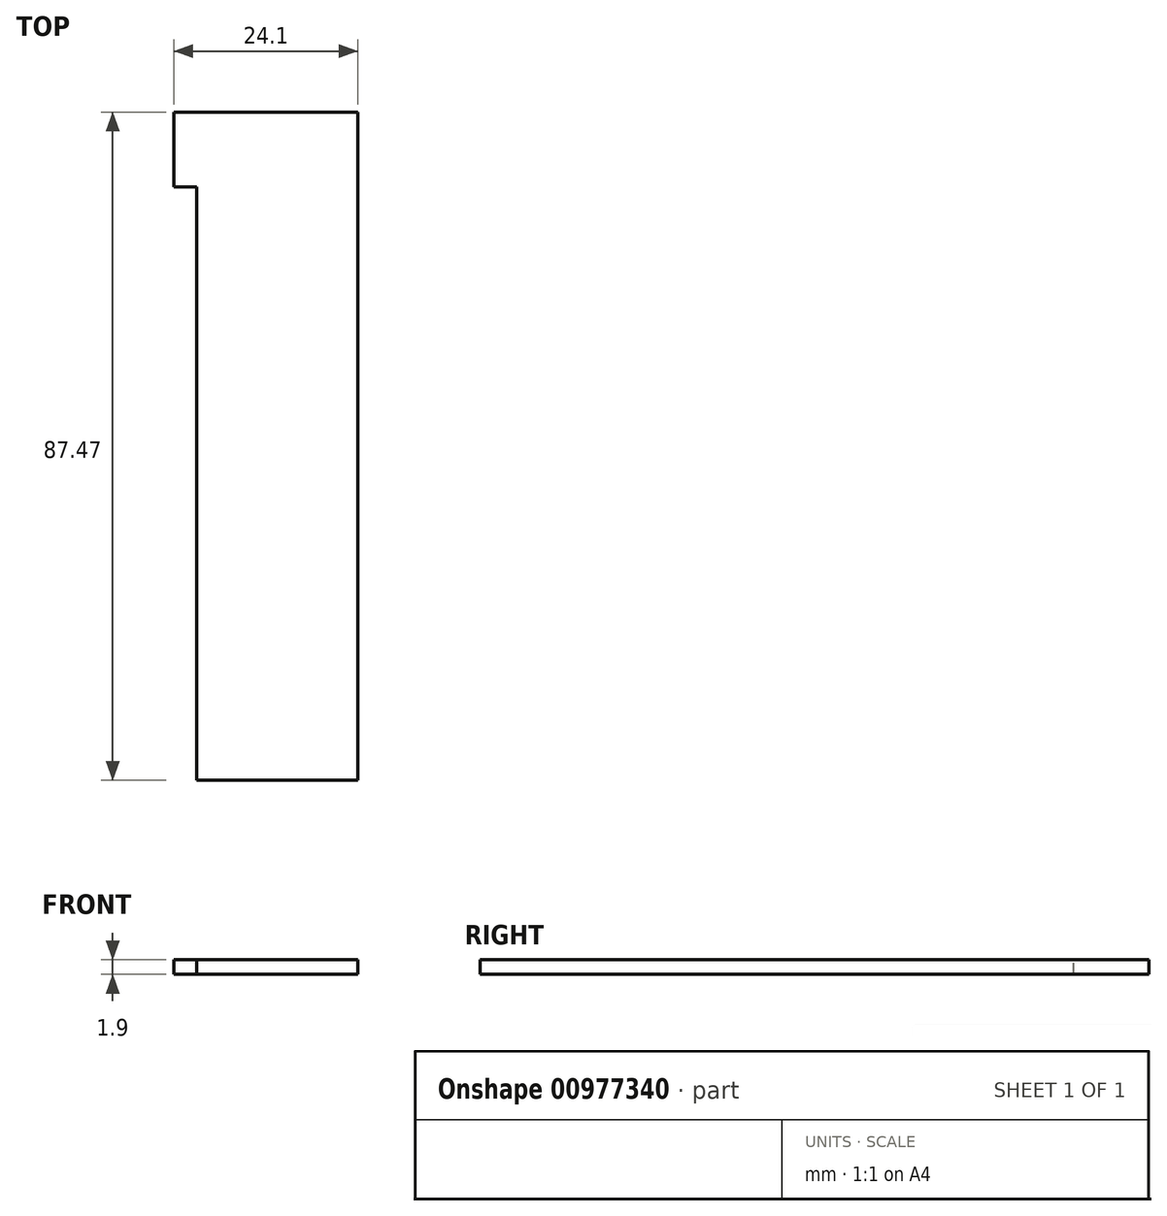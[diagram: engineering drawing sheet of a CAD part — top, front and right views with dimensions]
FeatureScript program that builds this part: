
annotation { "Feature Type Name" : "Feature", "Feature Type Description" : "" }
export const myFeature = defineFeature(function(context is Context, id is Id, definition is map)
    precondition{}
    {
        {
            var Q0;
            Q0=qCreatedBy(makeId("Top.planeOp"),FACE);
            var sketch = newSketch(context, id + "F0", { "sketchPlane" : qUnion([Q0])});
            skLineSegment(sketch, "E0.bottom", {"start": v(0, 0) * mm, "end": v(21.1, 0) * mm});
            skLineSegment(sketch, "E0.top", {"start": v(0, 87.47) * mm, "end": v(21.1, 87.47) * mm});
            skLineSegment(sketch, "E0.left", {"start": v(0, 0) * mm, "end": v(0, 87.47) * mm});
            skLineSegment(sketch, "E0.right", {"start": v(21.1, 0) * mm, "end": v(21.1, 87.47) * mm});
            skSolve(sketch);
        }
        {
            var Q0;
            Q0=qSketchRegion(id+"F0",true);
            extrude(context, id + "F1", {"entities" : qUnion([Q0]), "depth" : 1.9 * mm, "offsetDistance" : 25 * mm});
        }
        {
            var Q0;
            Q0=qCreatedBy(makeId("Top.planeOp"),FACE);
            var sketch = newSketch(context, id + "F2", { "sketchPlane" : qUnion([Q0])});
            skLineSegment(sketch, "E1.bottom", {"start": v(27.75, 86.65) * mm, "end": v(45.35, 86.65) * mm});
            skLineSegment(sketch, "E1.top", {"start": v(27.75, 2.88) * mm, "end": v(45.35, 2.88) * mm});
            skLineSegment(sketch, "E1.left", {"start": v(27.75, 86.65) * mm, "end": v(27.75, 2.88) * mm});
            skLineSegment(sketch, "E1.right", {"start": v(45.35, 86.65) * mm, "end": v(45.35, 2.88) * mm});
            skLineSegment(sketch, "E2.bottom", {"start": v(29.75, 84.65) * mm, "end": v(43.35, 84.65) * mm});
            skLineSegment(sketch, "E2.top", {"start": v(29.75, 4.88) * mm, "end": v(43.35, 4.88) * mm});
            skLineSegment(sketch, "E2.left", {"start": v(29.75, 84.65) * mm, "end": v(29.75, 4.88) * mm});
            skLineSegment(sketch, "E2.right", {"start": v(43.35, 84.65) * mm, "end": v(43.35, 4.88) * mm});
            skSolve(sketch);
        }
        {
            var Q0;
            Q0=qSketchRegion(id+"F2",true);
            extrude(context, id + "F3", {"entities" : qUnion([Q0]), "depth" : 0.8 * mm, "offsetDistance" : 25 * mm});
        }
        {
            var Q0;
            Q0=makeQuery(id+"F1.opExtrude","SWEPT_FACE",FACE,{"disambiguationData":[OSD([sQuery(id+"F0.wireOp",EDGE,"E0.left")])]});
            var sketch = newSketch(context, id + "F4", { "sketchPlane" : qUnion([Q0])});
            skLineSegment(sketch, "E3.bottom", {"start": v(-87.47, 0) * mm, "end": v(-77.67, 0) * mm});
            skLineSegment(sketch, "E3.top", {"start": v(-87.47, 1.9) * mm, "end": v(-77.67, 1.9) * mm});
            skLineSegment(sketch, "E3.left", {"start": v(-87.47, 0) * mm, "end": v(-87.47, 1.9) * mm});
            skLineSegment(sketch, "E3.right", {"start": v(-77.67, 0) * mm, "end": v(-77.67, 1.9) * mm});
            skSolve(sketch);
        }
        {
            var Q0;
            Q0=qSketchRegion(id+"F4",true);
            extrude(context, id + "F5", {"entities" : qUnion([Q0]), "operationType" : NewBodyOperationType.ADD, "depth" : 3 * mm, "offsetDistance" : 25 * mm});
        }
        {
            var Q0;
            Q0=makeQuery(id+"F3.opExtrude","SWEPT_BODY",BODY,{"disambiguationData":[OSD([sQuery(id+"F2.wireOp",EDGE,"E1.bottom"),sQuery(id+"F2.wireOp",EDGE,"E1.top"),sQuery(id+"F2.wireOp",EDGE,"E1.left"),sQuery(id+"F2.wireOp",EDGE,"E1.right"),sQuery(id+"F2.wireOp",EDGE,"E2.bottom"),sQuery(id+"F2.wireOp",EDGE,"E2.top"),sQuery(id+"F2.wireOp",EDGE,"E2.left"),sQuery(id+"F2.wireOp",EDGE,"E2.right")])]});
            deleteBodies(context, id + "F6", {"entities" : qUnion([Q0])});
        }
    });
